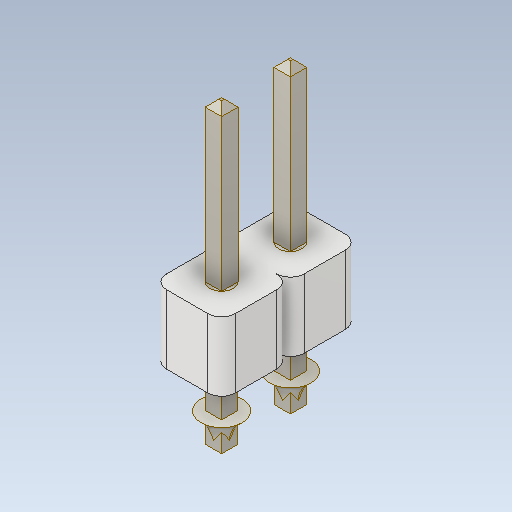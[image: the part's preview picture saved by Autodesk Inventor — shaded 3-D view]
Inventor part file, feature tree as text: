
AUTODESK INVENTOR PART (.ipt)
format: ipt  version: 2020 (Build 240168000, 168)  size: 526,336 bytes
history: native  units: in
note: dims shown in document units (in); Inventor stores cm internally (conversion verified against a paired STEP export)
features: other x53, sketch x7, extrude x4, plane x2, pattern_linear x2, chamfer x1, loft x1, projected_geometry x1
ambient origin geometry x8: Origin, YZ Plane, XZ Plane, XY Plane, X Axis, Y Axis, Z Axis, Center Point
bodies: Solid1 (feature_tree), Solid2 (feature_tree)
feature tree (71):
  other  "Table"
  other  "90 deg = Suppress"
  other  "90 deg = Compute"
  other  "Row = 5"
  other  "Row = 29"
  other  "Row = 37"
  other  "Row = 24"
  other  "Row = 14"
  other  "Row = 4"
  other  "Row = 7"
  other  "Row = 31"
  other  "Row = 9"
  other  "Column = 2"
  other  "Row = 22"
  other  "Row = 20"
  other  "Row = 12"
  other  "Row = 17"
  other  "Row = 15"
  other  "Row = 34"
  other  "Row = 11"
  other  "Row = 2"
  other  "Row = 40"
  other  "Row = 28"
  other  "Row = 25"
  other  "Column = 1"
  other  "Row = 1"
  other  "Row = 36"
  other  "Row = 16"
  other  "Row = 13"
  other  "Row = 33"
  other  "Row = 8"
  other  "Row = 6"
  other  "Row = 32"
  other  "Row = 27"
  other  "Row = 23"
  other  "Row = 21"
  other  "Row = 35"
  other  "Row = 30"
  other  "Row = 39"
  other  "Row = 38"
  other  "Row = 18"
  other  "Color = Smooth - Black"
  other  "Row = 19"
  other  "Row = 26"
  other  "Row = 10"
  other  "Color = Blue - Wall Paint - Glossy"
  other  "Row = 3"
  other  "Color = Yellow"
  other  "Color = Orange"
  other  "Color = Green"
  other  "Color = Red"
  other  "Color = White"
  extrude  "Extrusion1"  Depth=0.1in
  extrude  "Extrusion2"  Depth=0.02in
  extrude  "Extrusion3"  Depth=0.024in
  chamfer  "Chamfer1"  Distance=0.23in
  extrude  "Extrusion4"  Depth=0.023in
  plane  "Work Plane1"
  sketch  "Sketch6"  dims[d18=0.1in d19=0.7874in d21=0.1in]
  plane  "Work Plane2"
  loft  "Loft1"
  pattern_linear  "Rectangular Pattern1"  Count1=2 Spacing1=0.1in
  pattern_linear  "Rectangular Pattern2"  Spacing1=0.105in  [1 undecoded]
  other  "90 deg"
  sketch  "Sketch1"  dims[d0=0.1in d1=0.1in]
  sketch  "Sketch2"  dims[d2=0.02in d3=0.02in]
  sketch  "Sketch3"  dims[d4=0.1in d5=0.0in d6=0.024in d7=0.23in d8=0.0in]
  sketch  "Sketch4"  dims[d9=0.023in d10=0.023in]
  sketch  "Sketch5"  dims[d11=0.115in d12=0.0in d13=0.01in d14=0.125in d15=45.0deg]
  projected_geometry  "Projected Loop1"
  sketch  "Sketch7"  dims[d24=0.1in d25=0.3937in d27=0.1in d31=0.105in d32=0.0in d36=0.0125in d39=0.024in d41=0.124in d42=0.02in d43=90.0deg d44=0.0625in d45=0.06in d46=0.0312in d47=0.0in d48=90.0deg d49=0.3937in d50=90.0deg]
note: 1 required parameter value undecoded (feature->parameter linkage not recoverable at this tier; creation-order binding heuristic only, values carry confidence <= 0.55)
